# Revit family: Ladder_Crossover_FIXFAST_KOMBI-Step
name_source: partatom
category: Generic Models
units: mm (PartAtom-declared; Revit-internal decimal feet)

## family parameters
Always vertical = No
Can host rebar = No
Cut with Voids When Loaded = No
Maintain Annotation Orientation = No
OmniClass Number = 23.30.70.21
OmniClass Title = Stairs
Part Type = Normal
Room Calculation Point = No
Round Connector Dimension = Use Diameter
Shared = No
Work Plane-Based = Yes

## types (1)
- 65 Degree Incline
    Assembly Code = E1090900
    Capacity = Total Load 5000 lbs  ;  Concentrated Load 1000 lbs
    Construction Details = http://www.arcat.com
    Default Elevation = 0' - 0"
    Description = FIXFAST KOMBI Crossover Steps - as Specified
    Expected Lifespan (Years) = 0
    Green Building-LEED = http://www.arcat.com
    Keynote = 05 51 33
    Ladder Incline = 65.00°
    Maintenance Schedule (Months) = 0
    Manufacturer = FIXFAST USA
    Manufacturer Fax = 317-769-5560
    Manufacturer Website = http://www.fixfastusa.com
    Model = KOMBI Stairs
    Product Data = http://www.arcat.com
    Revision = R1_2017-06
    Sales Information = http://www.fixfastusa.com
    Specification = http://www.arcat.com
    Standards Conformance = OSHA 29 CFR 1910.25
    URL = http://www.fixfastusa.com
    Warranty Duration (Years) = 0

## geometry (parser evidence)
native form markers: Blend x6, Sweep x8
no freeform markers — native parametric forms only
